FCSTD DOCUMENT  (FreeCAD 0.19R24276 (Git))
Label: names
License: All rights reserved
LicenseURL: http://en.wikipedia.org/wiki/All_rights_reserved
objects: PartDesign::Body×2, Sketcher::SketchObject×1
note: 3 computed .brp shape members not serialized (recipe doc carries the construction recipe); baked Part::Feature solids carry a one-line shape summary decoded from their .brp

FEATURE [PartDesign::Body] Body
  Origin = -> Origin
FEATURE [Sketcher::SketchObject] Sketch
  FullyConstrained = false
  MapMode = 5
  Support = -> [XY_Plane001]
  sketch-geometry (20):
    g0: LineSegment StartX=0 StartY=0 StartZ=0 EndX=0 EndY=100 EndZ=0
    g1: LineSegment StartX=0 StartY=100 StartZ=0 EndX=20 EndY=100 EndZ=0
    g2: LineSegment StartX=0 StartY=0 StartZ=0 EndX=20 EndY=1.54756e-11 EndZ=0
    g3: LineSegment StartX=20 StartY=80 StartZ=0 EndX=20 EndY=20 EndZ=0
    g4: ArcOfCircle CenterX=20 CenterY=50 CenterZ=0 NormalX=0 NormalY=0 NormalZ=1 AngleXU=0 Radius=50 StartAngle=4.71239 EndAngle=7.85398
    g5: ArcOfCircle CenterX=20 CenterY=50 CenterZ=0 NormalX=0 NormalY=0 NormalZ=1 AngleXU=0 Radius=30 StartAngle=4.71239 EndAngle=7.85398
    g6: LineSegment StartX=80 StartY=0 StartZ=0 EndX=80 EndY=100 EndZ=0
    g7: LineSegment StartX=80 StartY=100 StartZ=0 EndX=110 EndY=100 EndZ=0
    g8: LineSegment StartX=80 StartY=0 StartZ=0 EndX=100 EndY=0 EndZ=0
    g9: LineSegment StartX=110 StartY=100 StartZ=0 EndX=123.397 EndY=50 EndZ=0
    g10: LineSegment StartX=123.397 StartY=50 StartZ=0 EndX=123.397 EndY=100 EndZ=0
    g11: LineSegment StartX=123.397 StartY=100 StartZ=0 EndX=143.397 EndY=100 EndZ=0
    g12: LineSegment StartX=143.397 StartY=100 StartZ=0 EndX=143.397 EndY=0 EndZ=0
    g13: LineSegment StartX=143.397 StartY=0 StartZ=0 EndX=113.397 EndY=0 EndZ=0
    g14: LineSegment StartX=100 StartY=0 StartZ=0 EndX=100 EndY=50 EndZ=0
    g15: LineSegment StartX=100 StartY=50 StartZ=0 EndX=113.397 EndY=0 EndZ=0
    g16: LineSegment StartX=-71.5488 StartY=200 StartZ=0 EndX=228.451 EndY=200 EndZ=0
    g17: LineSegment StartX=228.451 StartY=200 StartZ=0 EndX=228.451 EndY=-100 EndZ=0
    g18: LineSegment StartX=228.451 StartY=-100 StartZ=0 EndX=-71.5488 EndY=-100 EndZ=0
    g19: LineSegment StartX=-71.5488 StartY=-100 StartZ=0 EndX=-71.5488 EndY=200 EndZ=0
  constraints (59):
    c: Coincident(g0,g-1)
    c: PointOnObject(g0,g-2)
    c: DistanceY(g0,g0) = 100
    c: Coincident(g1,g0)
    c: Horizontal(g1)
    c: Coincident(g2,g0)
    c: PointOnObject(g2,g-1)
    c: Vertical(g3)
    c: Coincident(g4,g1)
    c: Coincident(g4,g2)
    c: Coincident(g5,g3)
    c: Coincident(g5,g3)
    c: Coincident(g4,g5)
    c: Radius(g4) = 50
    c: Radius(g5) = 30
    c: PointOnObject(g6,g-1)
    c: Vertical(g6)
    c: Coincident(g7,g6)
    c: Horizontal(g7)
    c: Coincident(g8,g6)
    c: PointOnObject(g8,g-1)
    c: Coincident(g9,g7)
    c: Coincident(g10,g9)
    c: Vertical(g10)
    c: Coincident(g11,g10)
    c: Horizontal(g11)
    c: Coincident(g12,g11)
    c: PointOnObject(g12,g-1)
    c: Vertical(g12)
    c: Coincident(g13,g12)
    c: Horizontal(g13)
    c: Coincident(g14,g8)
    c: Vertical(g14)
    c: Coincident(g15,g14)
    c: Horizontal(g14,g9)
    c: Equal(g13,g7)
    c: Equal(g8,g11)
    c: DistanceY(g12,g12) = 100
    c: Coincident(g15,g13)
    c: Angle(g14,g15) = 0.261799
    c: Angle(g10,g9) = 0.261799
    c: Horizontal(g6,g1)
    c: Vertical(g3,g1)
    c: Vertical(g3,g2)
    c: DistanceX(g0,g3) = 20
    c: DistanceX(g7,g7) = 30
    c: DistanceX(g11,g11) = 20
    c: Coincident(g16,g17)
    c: Coincident(g17,g18)
    c: Coincident(g18,g19)
    c: Coincident(g19,g16)
    c: Horizontal(g16)
    c: Horizontal(g18)
    c: Vertical(g17)
    c: Vertical(g19)
    c: DistanceX(g18,g18) = 300
    c: Equal(g18,g17)
    c: DistanceX(g3,g14) = 80
    c: DistanceY(g0,g16) = 100
FEATURE [PartDesign::Body] Body001
  Group = -> [Sketch]
  Origin = -> Origin001
